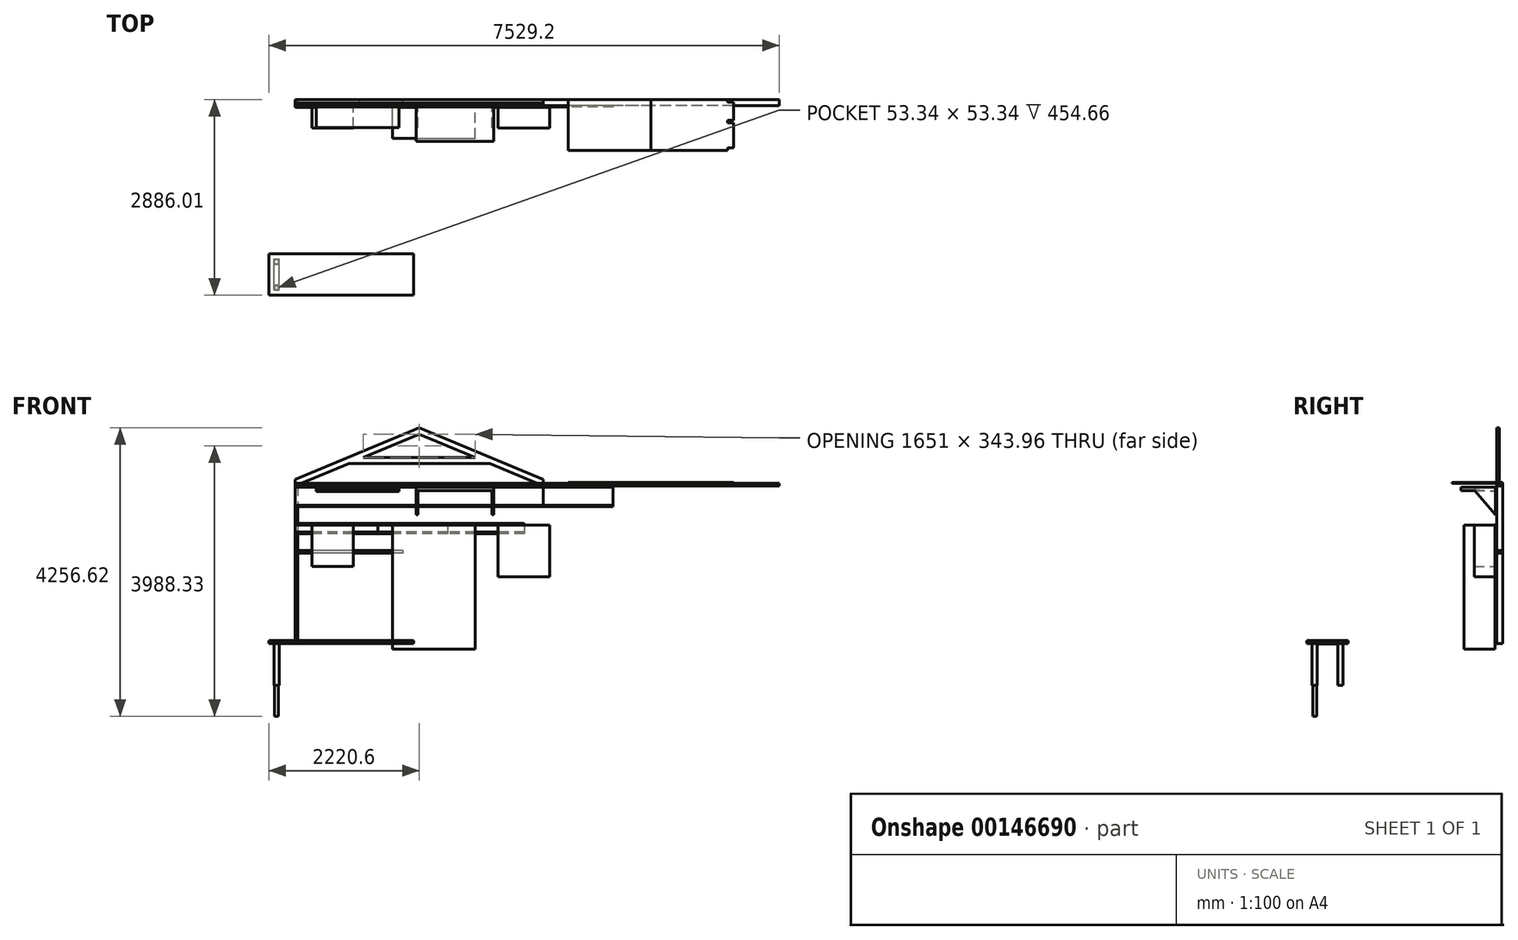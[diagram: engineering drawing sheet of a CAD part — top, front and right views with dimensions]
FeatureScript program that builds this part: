
annotation { "Feature Type Name" : "Feature", "Feature Type Description" : "" }
export const myFeature = defineFeature(function(context is Context, id is Id, definition is map)
    precondition{}
    {
        {
            var Q0;
            Q0=qCreatedBy(makeId("Top.planeOp"),FACE);
            var sketch = newSketch(context, id + "F0", { "sketchPlane" : qUnion([Q0])});
            skLineSegment(sketch, "E0.bottom", {"start": v(0, 0) * mm, "end": v(38.1, 0) * mm});
            skLineSegment(sketch, "E0.top", {"start": v(0, -88.9) * mm, "end": v(38.1, -88.9) * mm});
            skLineSegment(sketch, "E0.left", {"start": v(0, 0) * mm, "end": v(0, -88.9) * mm});
            skLineSegment(sketch, "E0.right", {"start": v(38.1, 0) * mm, "end": v(38.1, -88.9) * mm});
            skSolve(sketch);
        }
        {
            var Q0;
            Q0=makeQuery(id+"F0.imprint","IMPRINT",FACE,{"disambiguationData":[TD([[makeQuery(id+"F0.imprint","IMPRINT",EDGE,{"derivedFrom":sQuery(id+"F0.wireOp",EDGE,"E0.bottom")}),-1.0]])]});
            extrude(context, id + "F1", {"entities" : qUnion([Q0]), "depth" : 2324.1 * mm});
        }
        {
            var Q0;
            Q0=makeQuery(id+"F1.opExtrude","SWEPT_FACE",FACE,{"disambiguationData":[OSD([sQuery(id+"F0.wireOp",EDGE,"E0.left")])]});
            var sketch = newSketch(context, id + "F2", { "sketchPlane" : qUnion([Q0])});
            skLineSegment(sketch, "E1.bottom", {"start": v(0, 2324.1) * mm, "end": v(88.9, 2324.1) * mm});
            skLineSegment(sketch, "E1.top", {"start": v(0, 2362.2) * mm, "end": v(88.9, 2362.2) * mm});
            skLineSegment(sketch, "E1.left", {"start": v(0, 2324.1) * mm, "end": v(0, 2362.2) * mm});
            skLineSegment(sketch, "E1.right", {"start": v(88.9, 2324.1) * mm, "end": v(88.9, 2362.2) * mm});
            skSolve(sketch);
        }
        {
            var Q0;
            Q0 = qSketchRegion(id + "F2", true);
            extrude(context, id + "F3", {"entities" : qUnion([Q0]), "oppositeDirection" : true, "depth" : 3657.6 * mm});
        }
        {
            var Q0;
            Q0=makeQuery(id+"F1.opExtrude","SWEPT_FACE",FACE,{"disambiguationData":[OSD([sQuery(id+"F0.wireOp",EDGE,"E0.left")])]});
            var sketch = newSketch(context, id + "F4", { "sketchPlane" : qUnion([Q0])});
            skLineSegment(sketch, "E2", {"start": v(88.9, 2324.1) * mm, "end": v(107.95, 2305.05) * mm});
            skLineSegment(sketch, "E3", {"start": v(107.95, 2305.05) * mm, "end": v(107.95, 2038.35) * mm});
            skLineSegment(sketch, "E4", {"start": v(107.95, 2038.35) * mm, "end": v(88.9, 2019.3) * mm});
            skSolve(sketch);
        }
        {
            var Q0;
            {var subQ0=sQuery(id+"F4.wireOp",EDGE,"E2");Q0=makeQuery(id+"F4.imprint","IMPRINT",FACE,{"disambiguationData":[TD([[makeQuery(id+"F4.imprint","IMPRINT",EDGE,{"derivedFrom":subQ0}),-1.0]])]});}
            extrude(context, id + "F5", {"entities" : qUnion([Q0]), "oppositeDirection" : true, "depth" : 2438.4 * mm});
        }
        {
            var Q0;
            Q0=makeQuery(id+"F5.opExtrude","CAP_FACE",FACE,{"disambiguationData":[OSD([sQuery(id+"F0.wireOp",EDGE,"E0.top"),sQuery(id+"F0.wireOp",EDGE,"E0.left"),sQuery(id+"F4.wireOp",EDGE,"E2"),sQuery(id+"F4.wireOp",EDGE,"E3"),sQuery(id+"F4.wireOp",EDGE,"E4")])],"isStart":false});
            extrude(context, id + "F6", {"entities" : qUnion([Q0]), "depth" : 1219.2 * mm});
        }
        {
            var Q0;
            Q0=makeQuery(id+"F1.opExtrude","SWEPT_FACE",FACE,{"disambiguationData":[OSD([sQuery(id+"F0.wireOp",EDGE,"E0.left")])]});
            var sketch = newSketch(context, id + "F7", { "sketchPlane" : qUnion([Q0])});
            skLineSegment(sketch, "E5", {"start": v(88.9, 1772.5) * mm, "end": v(114.3, 1747.1) * mm});
            skLineSegment(sketch, "E6", {"start": v(114.3, 1747.1) * mm, "end": v(114.3, 1645.5) * mm});
            skLineSegment(sketch, "E7", {"start": v(114.3, 1645.5) * mm, "end": v(88.9, 1620.1) * mm});
            skSolve(sketch);
        }
        {
            var Q0;
            {var subQ0=sQuery(id+"F7.wireOp",EDGE,"E5");Q0=makeQuery(id+"F7.imprint","IMPRINT",FACE,{"disambiguationData":[TD([[makeQuery(id+"F7.imprint","IMPRINT",EDGE,{"derivedFrom":subQ0}),-1.0]])]});}
            extrude(context, id + "F8", {"entities" : qUnion([Q0]), "oppositeDirection" : true, "depth" : 1219.2 * mm});
        }
        {
            var Q0;
            Q0=makeQuery(id+"F1.opExtrude","SWEPT_FACE",FACE,{"disambiguationData":[OSD([sQuery(id+"F0.wireOp",EDGE,"E0.right")])]});
            var sketch = newSketch(context, id + "F9", { "sketchPlane" : qUnion([Q0])});
            skLineSegment(sketch, "E8.bottom", {"start": v(-88.9, 1368.17) * mm, "end": v(0, 1368.17) * mm});
            skLineSegment(sketch, "E8.top", {"start": v(-88.9, 1330.07) * mm, "end": v(0, 1330.07) * mm});
            skLineSegment(sketch, "E8.left", {"start": v(-88.9, 1368.17) * mm, "end": v(-88.9, 1330.07) * mm});
            skLineSegment(sketch, "E8.right", {"start": v(0, 1368.17) * mm, "end": v(0, 1330.07) * mm});
            skSolve(sketch);
        }
        {
            var Q0;
            Q0=makeQuery(id+"F9.imprint","IMPRINT",FACE,{"disambiguationData":[TD([[makeQuery(id+"F9.imprint","IMPRINT",EDGE,{"derivedFrom":sQuery(id+"F9.wireOp",EDGE,"E8.bottom")}),-1.0]])]});
            extrude(context, id + "F10", {"entities" : qUnion([Q0]), "depth" : 914.4 * mm});
        }
        {
            var Q0;
            Q0=makeQuery(id+"F6.opExtrude","CAP_FACE",FACE,{"disambiguationData":[OSD([sQuery(id+"F0.wireOp",EDGE,"E0.top"),sQuery(id+"F0.wireOp",EDGE,"E0.left"),sQuery(id+"F4.wireOp",EDGE,"E2"),sQuery(id+"F4.wireOp",EDGE,"E3"),sQuery(id+"F4.wireOp",EDGE,"E4")])],"isStart":false});
            extrude(context, id + "F11", {"entities" : qUnion([Q0]), "depth" : 1028.7 * mm});
        }
        {
            var Q0;
            Q0=makeQuery(id+"F8.opExtrude","CAP_FACE",FACE,{"disambiguationData":[OSD([sQuery(id+"F0.wireOp",EDGE,"E0.top"),sQuery(id+"F0.wireOp",EDGE,"E0.left"),sQuery(id+"F7.wireOp",EDGE,"E5"),sQuery(id+"F7.wireOp",EDGE,"E6"),sQuery(id+"F7.wireOp",EDGE,"E7")])],"isStart":false});
            extrude(context, id + "F12", {"entities" : qUnion([Q0]), "depth" : 1028.7 * mm});
        }
        {
            var Q0;
            Q0=makeQuery(id+"F8.opExtrude","SWEPT_FACE",FACE,{"disambiguationData":[OSD([sQuery(id+"F7.wireOp",EDGE,"E6")])]});
            var sketch = newSketch(context, id + "F13", { "sketchPlane" : qUnion([Q0])});
            skLineSegment(sketch, "E9.bottom", {"start": v(242.04, 1747.1) * mm, "end": v(851.64, 1747.1) * mm});
            skLineSegment(sketch, "E9.top", {"start": v(242.04, 1137.5) * mm, "end": v(851.64, 1137.5) * mm});
            skLineSegment(sketch, "E9.left", {"start": v(242.04, 1747.1) * mm, "end": v(242.04, 1137.5) * mm});
            skLineSegment(sketch, "E9.right", {"start": v(851.64, 1747.1) * mm, "end": v(851.64, 1137.5) * mm});
            skSolve(sketch);
        }
        {
            var Q0;
            Q0 = qSketchRegion(id + "F13", true);
            extrude(context, id + "F14", {"entities" : qUnion([Q0]), "depth" : 304.8 * mm});
        }
        {
            var Q0;
            Q0=makeQuery(id+"F12.opExtrude","SWEPT_FACE",FACE,{"disambiguationData":[OSD([sQuery(id+"F7.wireOp",EDGE,"E6")])]});
            var sketch = newSketch(context, id + "F15", { "sketchPlane" : qUnion([Q0])});
            skLineSegment(sketch, "E10.bottom", {"start": v(1434.78, 1747.1) * mm, "end": v(2653.98, 1747.1) * mm});
            skLineSegment(sketch, "E10.top", {"start": v(1434.78, -81.7) * mm, "end": v(2653.98, -81.7) * mm});
            skLineSegment(sketch, "E10.left", {"start": v(1434.78, 1747.1) * mm, "end": v(1434.78, -81.7) * mm});
            skLineSegment(sketch, "E10.right", {"start": v(2653.98, 1747.1) * mm, "end": v(2653.98, -81.7) * mm});
            skSolve(sketch);
        }
        {
            var Q0;
            Q0 = qSketchRegion(id + "F15", true);
            extrude(context, id + "F16", {"entities" : qUnion([Q0]), "depth" : 457.2 * mm});
        }
        {
            var Q0;
            Q0=makeQuery(id+"F12.opExtrude","SWEPT_FACE",FACE,{"disambiguationData":[OSD([sQuery(id+"F7.wireOp",EDGE,"E6")])]});
            var sketch = newSketch(context, id + "F17", { "sketchPlane" : qUnion([Q0])});
            skLineSegment(sketch, "E11.bottom", {"start": v(2987.72, 1747.1) * mm, "end": v(3749.72, 1747.1) * mm});
            skLineSegment(sketch, "E11.top", {"start": v(2987.72, 985.1) * mm, "end": v(3749.72, 985.1) * mm});
            skLineSegment(sketch, "E11.left", {"start": v(2987.72, 1747.1) * mm, "end": v(2987.72, 985.1) * mm});
            skLineSegment(sketch, "E11.right", {"start": v(3749.72, 1747.1) * mm, "end": v(3749.72, 985.1) * mm});
            skSolve(sketch);
        }
        {
            var Q0;
            Q0 = qSketchRegion(id + "F17", true);
            extrude(context, id + "F18", {"entities" : qUnion([Q0]), "depth" : 304.8 * mm});
        }
        {
            var Q0;
            Q0=makeQuery(id+"F5.opExtrude","SWEPT_FACE",FACE,{"disambiguationData":[OSD([sQuery(id+"F4.wireOp",EDGE,"E3")])]});
            var sketch = newSketch(context, id + "F19", { "sketchPlane" : qUnion([Q0])});
            skLineSegment(sketch, "E12.bottom", {"start": v(310.09, 2305.05) * mm, "end": v(1529.29, 2305.05) * mm});
            skLineSegment(sketch, "E12.top", {"start": v(310.09, 2241.55) * mm, "end": v(1529.29, 2241.55) * mm});
            skLineSegment(sketch, "E12.left", {"start": v(310.09, 2305.05) * mm, "end": v(310.09, 2241.55) * mm});
            skLineSegment(sketch, "E12.right", {"start": v(1529.29, 2305.05) * mm, "end": v(1529.29, 2241.55) * mm});
            skSolve(sketch);
        }
        {
            var Q0;
            Q0 = qSketchRegion(id + "F19", true);
            extrude(context, id + "F20", {"entities" : qUnion([Q0]), "depth" : 304.8 * mm});
        }
        {
            var Q0;
            Q0=makeQuery(id+"F20.opExtrude","SWEPT_FACE",FACE,{"disambiguationData":[OSD([sQuery(id+"F19.wireOp",EDGE,"E12.right")])]});
            var sketch = newSketch(context, id + "F21", { "sketchPlane" : qUnion([Q0])});
            skLineSegment(sketch, "E13", {"start": v(-412.75, 2273.3) * mm, "end": v(-107.95, 2241.55) * mm});
            skSolve(sketch);
        }
        {
            var Q0;
            {var subQ0=sQuery(id+"F21.wireOp",EDGE,"E13");Q0=makeQuery(id+"F21.imprint","IMPRINT",FACE,{"disambiguationData":[TD([[makeQuery(id+"F21.imprint","IMPRINT",EDGE,{"derivedFrom":subQ0}),-1.0]])]});}
            extrude(context, id + "F22", {"entities" : qUnion([Q0]), "operationType" : NewBodyOperationType.REMOVE, "endBound" : BoundingType.THROUGH_ALL, "oppositeDirection" : true, "depth" : 576.84 * mm});
        }
        {
            var Q0;
            Q0=makeQuery(id+"F5.opExtrude","SWEPT_FACE",FACE,{"disambiguationData":[OSD([sQuery(id+"F4.wireOp",EDGE,"E3")])]});
            var sketch = newSketch(context, id + "F23", { "sketchPlane" : qUnion([Q0])});
            skLineSegment(sketch, "E14.bottom", {"start": v(1779.4, 2305.05) * mm, "end": v(2922.4, 2305.05) * mm});
            skLineSegment(sketch, "E14.top", {"start": v(1779.4, 2254.25) * mm, "end": v(2922.4, 2254.25) * mm});
            skLineSegment(sketch, "E14.left", {"start": v(1779.4, 2305.05) * mm, "end": v(1779.4, 2254.25) * mm});
            skLineSegment(sketch, "E14.right", {"start": v(2922.4, 2305.05) * mm, "end": v(2922.4, 2254.25) * mm});
            skSolve(sketch);
        }
        {
            var Q0;
            Q0 = qSketchRegion(id + "F23", true);
            extrude(context, id + "F24", {"entities" : qUnion([Q0]), "depth" : 508 * mm});
        }
        {
            var Q0;
            Q0=makeQuery(id+"F24.opExtrude","SWEPT_FACE",FACE,{"disambiguationData":[OSD([sQuery(id+"F23.wireOp",EDGE,"E14.right")])]});
            var sketch = newSketch(context, id + "F25", { "sketchPlane" : qUnion([Q0])});
            skLineSegment(sketch, "E15", {"start": v(-107.95, 2254.25) * mm, "end": v(-107.95, 1898.65) * mm});
            skLineSegment(sketch, "E16", {"start": v(-107.95, 1898.65) * mm, "end": v(-412.75, 2254.25) * mm});
            skSolve(sketch);
        }
        {
            var Q0;
            {var subQ0=sQuery(id+"F25.wireOp",EDGE,"E15");Q0=makeQuery(id+"F25.imprint","IMPRINT",FACE,{"disambiguationData":[TD([[makeQuery(id+"F25.imprint","IMPRINT",EDGE,{"derivedFrom":subQ0}),-1.0]])]});}
            extrude(context, id + "F26", {"entities" : qUnion([Q0]), "operationType" : NewBodyOperationType.ADD, "oppositeDirection" : true, "depth" : 25.4 * mm});
        }
        {
            var Q0;
            Q0=makeQuery(id+"F24.opExtrude","SWEPT_FACE",FACE,{"disambiguationData":[OSD([sQuery(id+"F23.wireOp",EDGE,"E14.left")])]});
            var sketch = newSketch(context, id + "F27", { "sketchPlane" : qUnion([Q0])});
            skLineSegment(sketch, "E17.0", {"start": v(107.95, 1898.65) * mm, "end": v(412.75, 2254.25) * mm});
            skLineSegment(sketch, "E18.0", {"start": v(107.95, 2254.25) * mm, "end": v(107.95, 1898.65) * mm});
            skSolve(sketch);
        }
        {
            var Q0;
            {var subQ0=sQuery(id+"F27.wireOp",EDGE,"E17.0");Q0=makeQuery(id+"F27.imprint","IMPRINT",FACE,{"disambiguationData":[TD([[makeQuery(id+"F27.imprint","IMPRINT",EDGE,{"derivedFrom":subQ0}),1.0]])]});}
            extrude(context, id + "F28", {"entities" : qUnion([Q0]), "operationType" : NewBodyOperationType.ADD, "oppositeDirection" : true, "depth" : 25.4 * mm});
        }
        {
            var Q0;
            Q0=makeQuery(id+"F12.opExtrude","CAP_FACE",FACE,{"disambiguationData":[OSD([sQuery(id+"F0.wireOp",EDGE,"E0.top"),sQuery(id+"F0.wireOp",EDGE,"E0.left"),sQuery(id+"F7.wireOp",EDGE,"E5"),sQuery(id+"F7.wireOp",EDGE,"E6"),sQuery(id+"F7.wireOp",EDGE,"E7")])],"isStart":false});
            extrude(context, id + "F29", {"entities" : qUnion([Q0]), "depth" : 1130.3 * mm});
        }
        {
            var Q0;
            Q0=makeQuery(id+"F3.opExtrude","SWEPT_FACE",FACE,{"disambiguationData":[OSD([sQuery(id+"F2.wireOp",EDGE,"E1.top")])]});
            var sketch = newSketch(context, id + "F30", { "sketchPlane" : qUnion([Q0])});
            skLineSegment(sketch, "E19.bottom", {"start": v(4025.13, 0) * mm, "end": v(5244.33, 0) * mm});
            skLineSegment(sketch, "E19.top", {"start": v(4025.13, -749.3) * mm, "end": v(5244.33, -749.3) * mm});
            skLineSegment(sketch, "E19.left", {"start": v(4025.13, 0) * mm, "end": v(4025.13, -749.3) * mm});
            skLineSegment(sketch, "E19.right", {"start": v(5244.33, 0) * mm, "end": v(5244.33, -749.3) * mm});
            skSolve(sketch);
        }
        {
            var Q0;
            Q0 = qSketchRegion(id + "F30", true);
            extrude(context, id + "F31", {"entities" : qUnion([Q0]), "depth" : 12.7 * mm});
        }
        {
            var Q0;
            Q0=makeQuery(id+"F3.opExtrude","CAP_FACE",FACE,{"disambiguationData":[OSD([sQuery(id+"F2.wireOp",EDGE,"E1.bottom"),sQuery(id+"F2.wireOp",EDGE,"E1.top"),sQuery(id+"F2.wireOp",EDGE,"E1.left"),sQuery(id+"F2.wireOp",EDGE,"E1.right")])],"isStart":false});
            extrude(context, id + "F32", {"entities" : qUnion([Q0]), "depth" : 3479.8 * mm});
        }
        {
            var Q0;
            Q0=makeQuery(id+"F31.opExtrude","SWEPT_FACE",FACE,{"disambiguationData":[OSD([sQuery(id+"F30.wireOp",EDGE,"E19.right")])]});
            extrude(context, id + "F33", {"entities" : qUnion([Q0]), "depth" : 1130.3 * mm});
        }
        {
            var Q0;
            Q0=makeQuery(id+"F10.opExtrude","CAP_FACE",FACE,{"disambiguationData":[OSD([sQuery(id+"F9.wireOp",EDGE,"E8.bottom"),sQuery(id+"F9.wireOp",EDGE,"E8.top"),sQuery(id+"F9.wireOp",EDGE,"E8.left"),sQuery(id+"F9.wireOp",EDGE,"E8.right")])],"isStart":false});
            extrude(context, id + "F34", {"entities" : qUnion([Q0]), "depth" : 635 * mm});
        }
        {
            var Q0;
            Q0=makeQuery(id+"F33.opExtrude","CAP_FACE",FACE,{"disambiguationData":[OSD([sQuery(id+"F30.wireOp",EDGE,"E19.right")])],"isStart":false});
            var sketch = newSketch(context, id + "F35", { "sketchPlane" : qUnion([Q0])});
            skLineSegment(sketch, "E20.bottom", {"start": v(-38.1, 2374.9) * mm, "end": v(-304.8, 2374.9) * mm});
            skLineSegment(sketch, "E20.top", {"start": v(-38.1, 2362.2) * mm, "end": v(-304.8, 2362.2) * mm});
            skLineSegment(sketch, "E20.left", {"start": v(-38.1, 2374.9) * mm, "end": v(-38.1, 2362.2) * mm});
            skLineSegment(sketch, "E20.right", {"start": v(-304.8, 2374.9) * mm, "end": v(-304.8, 2362.2) * mm});
            skLineSegment(sketch, "E21.bottom", {"start": v(-342.9, 2374.9) * mm, "end": v(-711.2, 2374.9) * mm});
            skLineSegment(sketch, "E21.top", {"start": v(-342.9, 2362.2) * mm, "end": v(-711.2, 2362.2) * mm});
            skLineSegment(sketch, "E21.left", {"start": v(-342.9, 2374.9) * mm, "end": v(-342.9, 2362.2) * mm});
            skLineSegment(sketch, "E21.right", {"start": v(-711.2, 2374.9) * mm, "end": v(-711.2, 2362.2) * mm});
            skSolve(sketch);
        }
        {
            var Q0;
            Q0 = qSketchRegion(id + "F35", true);
            extrude(context, id + "F36", {"entities" : qUnion([Q0]), "operationType" : NewBodyOperationType.ADD, "depth" : 88.9 * mm});
        }
        {
            var Q0;
            Q0=qCreatedBy(makeId("Top.planeOp"),FACE);
            var sketch = newSketch(context, id + "F37", { "sketchPlane" : qUnion([Q0])});
            skLineSegment(sketch, "E22.bottom", {"start": v(-391.8, -2276.41) * mm, "end": v(1741.8, -2276.41) * mm});
            skLineSegment(sketch, "E22.top", {"start": v(-391.8, -2886.01) * mm, "end": v(1741.8, -2886.01) * mm});
            skLineSegment(sketch, "E22.left", {"start": v(-391.8, -2276.41) * mm, "end": v(-391.8, -2886.01) * mm});
            skLineSegment(sketch, "E22.right", {"start": v(1741.8, -2276.41) * mm, "end": v(1741.8, -2886.01) * mm});
            skSolve(sketch);
        }
        {
            var Q0;
            Q0 = qSketchRegion(id + "F37", true);
            extrude(context, id + "F38", {"entities" : qUnion([Q0]), "depth" : 44.45 * mm});
        }
        {
            var Q0;
            Q0=makeQuery(id+"F3.opExtrude","SWEPT_FACE",FACE,{"disambiguationData":[OSD([sQuery(id+"F2.wireOp",EDGE,"E1.right")])]});
            var sketch = newSketch(context, id + "F39", { "sketchPlane" : qUnion([Q0])});
            skLineSegment(sketch, "E23", {"start": v(0, 2421.47) * mm, "end": v(1828.8, 3183.47) * mm});
            skLineSegment(sketch, "E24", {"start": v(1828.8, 3183.47) * mm, "end": v(3657.6, 2421.47) * mm});
            skLineSegment(sketch, "E25", {"start": v(1828.8, 2362.2) * mm, "end": v(1828.8, 3183.47) * mm});
            skLineSegment(sketch, "E26", {"start": v(88.9, 2362.2) * mm, "end": v(1828.8, 3087.16) * mm});
            skLineSegment(sketch, "E27", {"start": v(1828.8, 3087.16) * mm, "end": v(3568.7, 2362.2) * mm});
            skLineSegment(sketch, "E28", {"start": v(1003.3, 2743.2) * mm, "end": v(2654.3, 2743.2) * mm});
            skLineSegment(sketch, "E29", {"start": v(2867.66, 2654.3) * mm, "end": v(789.94, 2654.3) * mm});
            skLineSegment(sketch, "E30", {"start": v(3657.6, 2421.47) * mm, "end": v(3657.6, 2362.2) * mm});
            skLineSegment(sketch, "E31", {"start": v(0, 2421.47) * mm, "end": v(0, 2362.2) * mm});
            skLineSegment(sketch, "E32", {"start": v(3568.7, 2362.2) * mm, "end": v(3263.9, 2362.2) * mm});
            skLineSegment(sketch, "E33", {"start": v(3263.9, 2362.2) * mm, "end": v(3263.9, 2489.2) * mm});
            skSolve(sketch);
        }
        {
            var Q0;
            {var subQ0=sQuery(id+"F39.wireOp",EDGE,"E23");Q0=makeQuery(id+"F39.imprint","IMPRINT",FACE,{"disambiguationData":[TD([[makeQuery(id+"F39.imprint","IMPRINT",EDGE,{"derivedFrom":subQ0}),-1.0]])]});}
            var Q1;
            {var subQ0=sQuery(id+"F39.wireOp",EDGE,"E24");Q1=makeQuery(id+"F39.imprint","IMPRINT",FACE,{"disambiguationData":[TD([[makeQuery(id+"F39.imprint","IMPRINT",EDGE,{"derivedFrom":subQ0}),-1.0]])]});}
            var Q2;
            {var subQ0=sQuery(id+"F39.wireOp",EDGE,"E29");var subQ1=sQuery(id+"F39.wireOp",EDGE,"E25");var subQ2=makeQuery(id+"F39.imprint","INTERSECT",VERTEX,{"derivedFrom":[subQ1,subQ0]});Q2=makeQuery(id+"F39.imprint","IMPRINT",FACE,{"disambiguationData":[TD([[makeQuery(id+"F39.imprint","IMPRINT",EDGE,{"disambiguationData":[TD([[subQ2,-1.0]])],"derivedFrom":subQ1}),-1.0]])]});}
            var Q3;
            {var subQ0=sQuery(id+"F39.wireOp",EDGE,"E29");var subQ1=sQuery(id+"F39.wireOp",EDGE,"E25");var subQ2=makeQuery(id+"F39.imprint","INTERSECT",VERTEX,{"derivedFrom":[subQ1,subQ0]});Q3=makeQuery(id+"F39.imprint","IMPRINT",FACE,{"disambiguationData":[TD([[makeQuery(id+"F39.imprint","IMPRINT",EDGE,{"disambiguationData":[TD([[subQ2,-1.0]])],"derivedFrom":subQ1}),1.0]])]});}
            extrude(context, id + "F40", {"entities" : qUnion([Q0, Q1, Q2, Q3]), "oppositeDirection" : true, "depth" : 38.1 * mm});
        }
        {
            var Q0;
            Q0=makeQuery(id+"F38.opExtrude","CAP_FACE",FACE,{"disambiguationData":[OSD([sQuery(id+"F37.wireOp",EDGE,"E22.bottom"),sQuery(id+"F37.wireOp",EDGE,"E22.top"),sQuery(id+"F37.wireOp",EDGE,"E22.left"),sQuery(id+"F37.wireOp",EDGE,"E22.right")])],"isStart":true});
            var sketch = newSketch(context, id + "F41", { "sketchPlane" : qUnion([Q0])});
            skLineSegment(sketch, "E34.bottom", {"start": v(-315.6, 2809.81) * mm, "end": v(-239.4, 2809.81) * mm});
            skLineSegment(sketch, "E34.top", {"start": v(-315.6, 2352.61) * mm, "end": v(-239.4, 2352.61) * mm});
            skLineSegment(sketch, "E34.left", {"start": v(-315.6, 2809.81) * mm, "end": v(-315.6, 2352.61) * mm});
            skLineSegment(sketch, "E34.right", {"start": v(-239.4, 2809.81) * mm, "end": v(-239.4, 2352.61) * mm});
            skLineSegment(sketch, "E35", {"start": v(-315.6, 2581.21) * mm, "end": v(-391.8, 2581.21) * mm});
            skSolve(sketch);
        }
        {
            var Q0;
            Q0 = qSketchRegion(id + "F41", true);
            extrude(context, id + "F42", {"entities" : qUnion([Q0]), "depth" : 6.35 * mm});
        }
        {
            var Q0;
            Q0=makeQuery(id+"F42.opExtrude","CAP_FACE",FACE,{"disambiguationData":[OSD([sQuery(id+"F41.wireOp",EDGE,"E34.bottom"),sQuery(id+"F41.wireOp",EDGE,"E34.top"),sQuery(id+"F41.wireOp",EDGE,"E34.left"),sQuery(id+"F41.wireOp",EDGE,"E34.right")])],"isStart":false});
            var sketch = newSketch(context, id + "F43", { "sketchPlane" : qUnion([Q0])});
            skLineSegment(sketch, "E36.bottom", {"start": v(-315.6, 2809.81) * mm, "end": v(-239.4, 2809.81) * mm});
            skLineSegment(sketch, "E36.top", {"start": v(-315.6, 2733.61) * mm, "end": v(-239.4, 2733.61) * mm});
            skLineSegment(sketch, "E36.left", {"start": v(-315.6, 2809.81) * mm, "end": v(-315.6, 2733.61) * mm});
            skLineSegment(sketch, "E36.right", {"start": v(-239.4, 2809.81) * mm, "end": v(-239.4, 2733.61) * mm});
            skLineSegment(sketch, "E37.bottom", {"start": v(-315.6, 2352.61) * mm, "end": v(-239.4, 2352.61) * mm});
            skLineSegment(sketch, "E37.top", {"start": v(-315.6, 2428.81) * mm, "end": v(-239.4, 2428.81) * mm});
            skLineSegment(sketch, "E37.left", {"start": v(-315.6, 2352.61) * mm, "end": v(-315.6, 2428.81) * mm});
            skLineSegment(sketch, "E37.right", {"start": v(-239.4, 2352.61) * mm, "end": v(-239.4, 2428.81) * mm});
            skSolve(sketch);
        }
        {
            var Q0;
            Q0 = qSketchRegion(id + "F43", true);
            extrude(context, id + "F44", {"entities" : qUnion([Q0]), "operationType" : NewBodyOperationType.ADD, "depth" : 609.6 * mm});
        }
        {
            var Q0;
            Q0=makeQuery(id+"F44.opExtrude","CAP_FACE",FACE,{"disambiguationData":[OSD([sQuery(id+"F43.wireOp",EDGE,"E36.bottom"),sQuery(id+"F43.wireOp",EDGE,"E36.top"),sQuery(id+"F43.wireOp",EDGE,"E36.left"),sQuery(id+"F43.wireOp",EDGE,"E36.right")])],"isStart":false});
            var Q1;
            Q1=makeQuery(id+"F44.opExtrude","CAP_FACE",FACE,{"disambiguationData":[OSD([sQuery(id+"F43.wireOp",EDGE,"E37.bottom"),sQuery(id+"F43.wireOp",EDGE,"E37.top"),sQuery(id+"F43.wireOp",EDGE,"E37.left"),sQuery(id+"F43.wireOp",EDGE,"E37.right")])],"isStart":false});
            shell(context, id + "F45", {"entities" : qUnion([Q0, Q1]), "thickness" : 6.35 * mm});
        }
        {
            var Q0;
            Q0=makeQuery(id+"F44.opExtrude","CAP_FACE",FACE,{"disambiguationData":[OSD([sQuery(id+"F43.wireOp",EDGE,"E36.bottom"),sQuery(id+"F43.wireOp",EDGE,"E36.top"),sQuery(id+"F43.wireOp",EDGE,"E36.left"),sQuery(id+"F43.wireOp",EDGE,"E36.right")])],"isStart":false});
            var sketch = newSketch(context, id + "F46", { "sketchPlane" : qUnion([Q0])});
            skLineSegment(sketch, "E38.0", {"start": v(-306.71, 2800.92) * mm, "end": v(-248.3, 2800.92) * mm});
            skLineSegment(sketch, "E38.1", {"start": v(-306.71, 2800.92) * mm, "end": v(-306.71, 2742.5) * mm});
            skLineSegment(sketch, "E38.2", {"start": v(-306.71, 2742.5) * mm, "end": v(-248.3, 2742.5) * mm});
            skLineSegment(sketch, "E38.3", {"start": v(-248.3, 2800.92) * mm, "end": v(-248.3, 2742.5) * mm});
            skSolve(sketch);
        }
        {
            var Q0;
            Q0 = qSketchRegion(id + "F46", true);
            extrude(context, id + "F47", {"entities" : qUnion([Q0]), "depth" : 457.2 * mm});
        }
        {
            var Q0;
            Q0=makeQuery(id+"F47.opExtrude","CAP_FACE",FACE,{"disambiguationData":[OSD([sQuery(id+"F46.wireOp",EDGE,"E38.0"),sQuery(id+"F46.wireOp",EDGE,"E38.1"),sQuery(id+"F46.wireOp",EDGE,"E38.2"),sQuery(id+"F46.wireOp",EDGE,"E38.3")])],"isStart":true});
            shell(context, id + "F48", {"entities" : qUnion([Q0]), "thickness" : 2.54 * mm});
        }
    });
